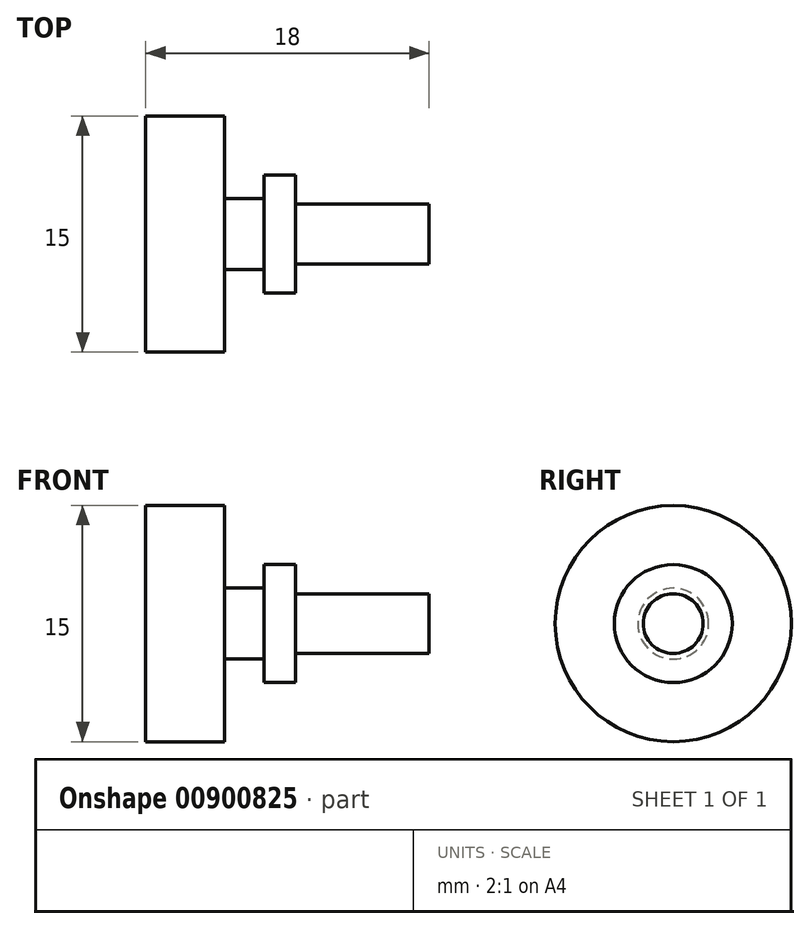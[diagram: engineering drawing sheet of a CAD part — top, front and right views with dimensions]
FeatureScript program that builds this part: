
annotation { "Feature Type Name" : "Feature", "Feature Type Description" : "" }
export const myFeature = defineFeature(function(context is Context, id is Id, definition is map)
    precondition{}
    {
        {
            var Q0;
            Q0=qCreatedBy(makeId("Front.planeOp"),FACE);
            var sketch = newSketch(context, id + "F0", { "sketchPlane" : qUnion([Q0])});
            skLineSegment(sketch, "E0.bottom", {"start": v(-42.83, 42.4) * mm, "end": v(-37.83, 42.4) * mm});
            skLineSegment(sketch, "E0.top", {"start": v(-42.83, 27.4) * mm, "end": v(-37.83, 27.4) * mm});
            skLineSegment(sketch, "E0.left", {"start": v(-42.83, 42.4) * mm, "end": v(-42.83, 27.4) * mm});
            skPoint(sketch, "E0.middle", {"position": v(-40.33, 34.9) * mm});
            skLineSegment(sketch, "E1.bottom", {"start": v(-37.83, 37.15) * mm, "end": v(-35.33, 37.15) * mm});
            skLineSegment(sketch, "E1.top", {"start": v(-37.83, 32.65) * mm, "end": v(-35.33, 32.65) * mm});
            skPoint(sketch, "E1.middle", {"position": v(-36.58, 34.9) * mm});
            skPoint(sketch, "E1.middle.positionSnap0", {"position": v(-37.83, 34.9) * mm});
            skPoint(sketch, "E1.centerSnap0", {"position": v(-37.83, 34.9) * mm});
            skLineSegment(sketch, "E2.bottom", {"start": v(-35.33, 38.65) * mm, "end": v(-33.33, 38.65) * mm});
            skLineSegment(sketch, "E2.top", {"start": v(-35.33, 31.15) * mm, "end": v(-33.33, 31.15) * mm});
            skPoint(sketch, "E2.middle", {"position": v(-34.33, 34.9) * mm});
            skLineSegment(sketch, "E3.bottom", {"start": v(-24.83, 36.8) * mm, "end": v(-33.33, 36.8) * mm});
            skLineSegment(sketch, "E3.top", {"start": v(-24.83, 33) * mm, "end": v(-33.33, 33) * mm});
            skLineSegment(sketch, "E3.left", {"start": v(-24.83, 36.8) * mm, "end": v(-24.83, 33) * mm});
            skPoint(sketch, "E3.middle", {"position": v(-29.08, 34.9) * mm});
            skLineSegment(sketch, "E4", {"start": v(-35.33, 37.15) * mm, "end": v(-35.33, 38.65) * mm});
            skLineSegment(sketch, "E5", {"start": v(-35.33, 32.65) * mm, "end": v(-35.33, 31.15) * mm});
            skLineSegment(sketch, "E6", {"start": v(-37.83, 37.15) * mm, "end": v(-37.83, 42.4) * mm});
            skLineSegment(sketch, "E7", {"start": v(-37.83, 32.65) * mm, "end": v(-37.83, 27.4) * mm});
            skLineSegment(sketch, "E8", {"start": v(-33.33, 36.8) * mm, "end": v(-33.33, 38.65) * mm});
            skLineSegment(sketch, "E9", {"start": v(-33.33, 33) * mm, "end": v(-33.33, 31.15) * mm});
            skLineSegment(sketch, "E10", {"start": v(-46.1, 34.9) * mm, "end": v(-16.76, 34.9) * mm});
            skSolve(sketch);
        }
        {
            var Q0;
            {var subQ1=sQuery(id+"F0.wireOp",EDGE,"E0.bottom");Q0=makeQuery(id+"F0.imprint","IMPRINT",FACE,{"disambiguationData":[TD([[makeQuery(id+"F0.imprint","IMPRINT",EDGE,{"derivedFrom":subQ1}),-1.0]])]});}
            var Q1;
            Q1=sQuery(id+"F0.wireOp",EDGE,"E10");
            revolve(context, id + "F1", {"surfaceOperationType" : NewSurfaceOperationType.NEW, "entities" : qUnion([Q0]), "axis" : qUnion([Q1]), "revolveType" : RevolveType.FULL});
        }
    });
